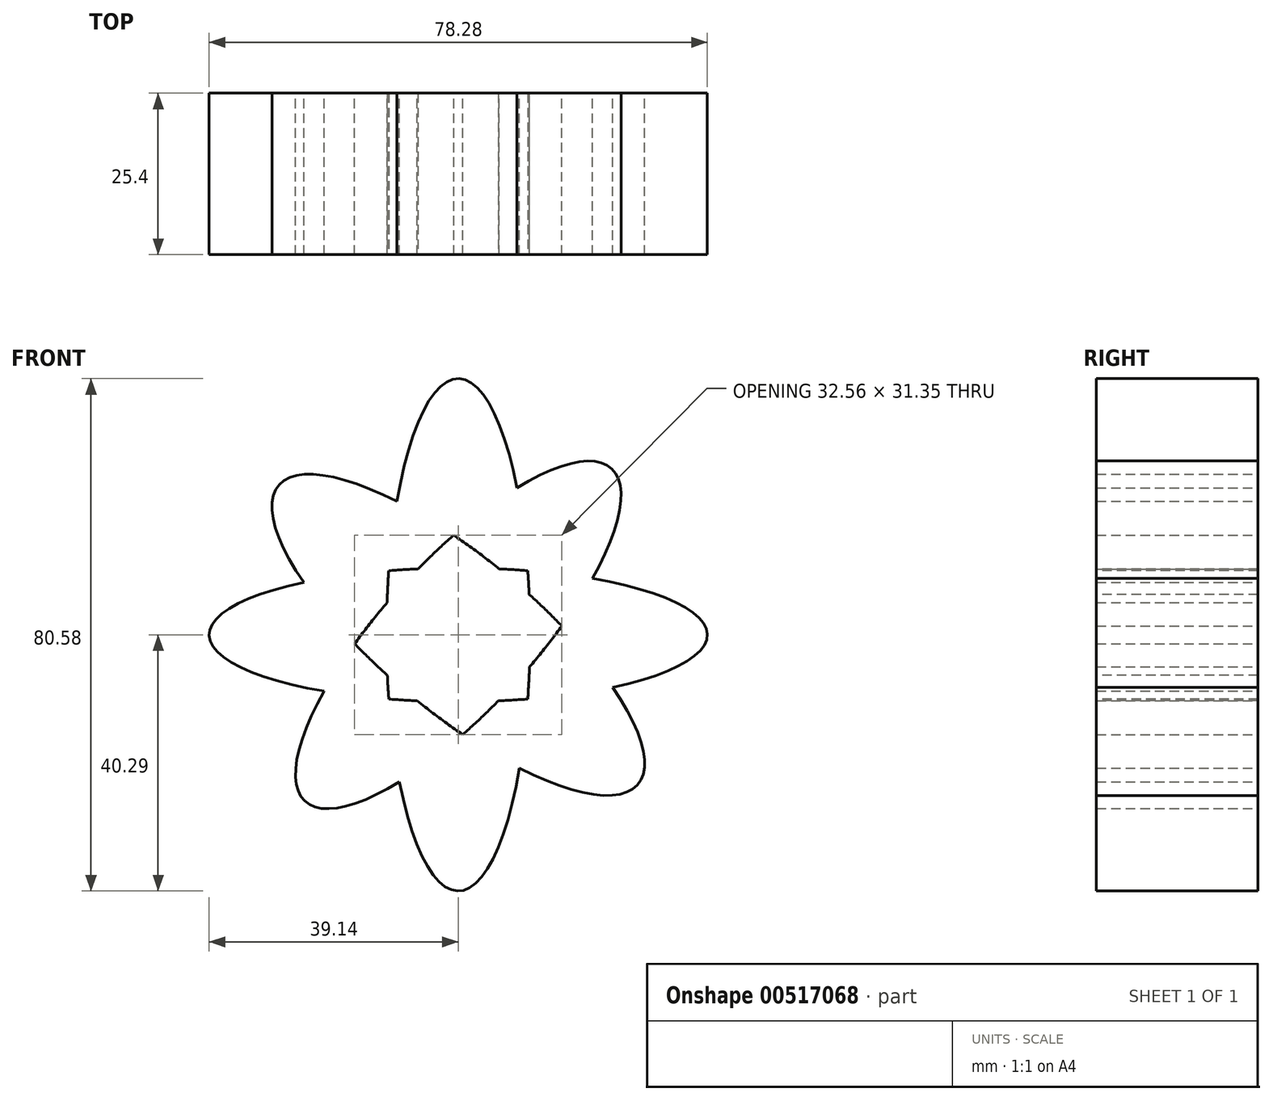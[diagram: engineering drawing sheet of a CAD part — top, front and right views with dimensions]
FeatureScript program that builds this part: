
annotation { "Feature Type Name" : "Feature", "Feature Type Description" : "" }
export const myFeature = defineFeature(function(context is Context, id is Id, definition is map)
    precondition{}
    {
        {
            var Q0;
            Q0=qCreatedBy(makeId("Front.planeOp"),FACE);
            var sketch = newSketch(context, id + "F0", { "sketchPlane" : qUnion([Q0])});
            skEllipse(sketch, "E0", {"center": v(0, 0) * mm, "majorRadius": 36.74 * mm, "minorRadius": 12.1 * mm, "majorAxis": v(-0.77, 0.64)});
            skEllipse(sketch, "E1", {"center": v(0, 0) * mm, "majorRadius": 35.56 * mm, "minorRadius": 11.72 * mm, "majorAxis": v(0.68, 0.74)});
            skEllipse(sketch, "E2", {"center": v(0, 0) * mm, "majorRadius": 39.14 * mm, "minorRadius": 10.51 * mm, "majorAxis": v(-1, 0)});
            skEllipse(sketch, "E3", {"center": v(0, 0) * mm, "majorRadius": 40.3 * mm, "minorRadius": 11.28 * mm, "majorAxis": v(0, 1)});
            skSolve(sketch);
        }
        {
            var Q0;
            Q0 = qSketchRegion(id + "F0", true);
            extrude(context, id + "F1", {"entities" : qUnion([Q0]), "depth" : 25.4 * mm, "offsetDistance" : 25.4 * mm});
        }
    });
